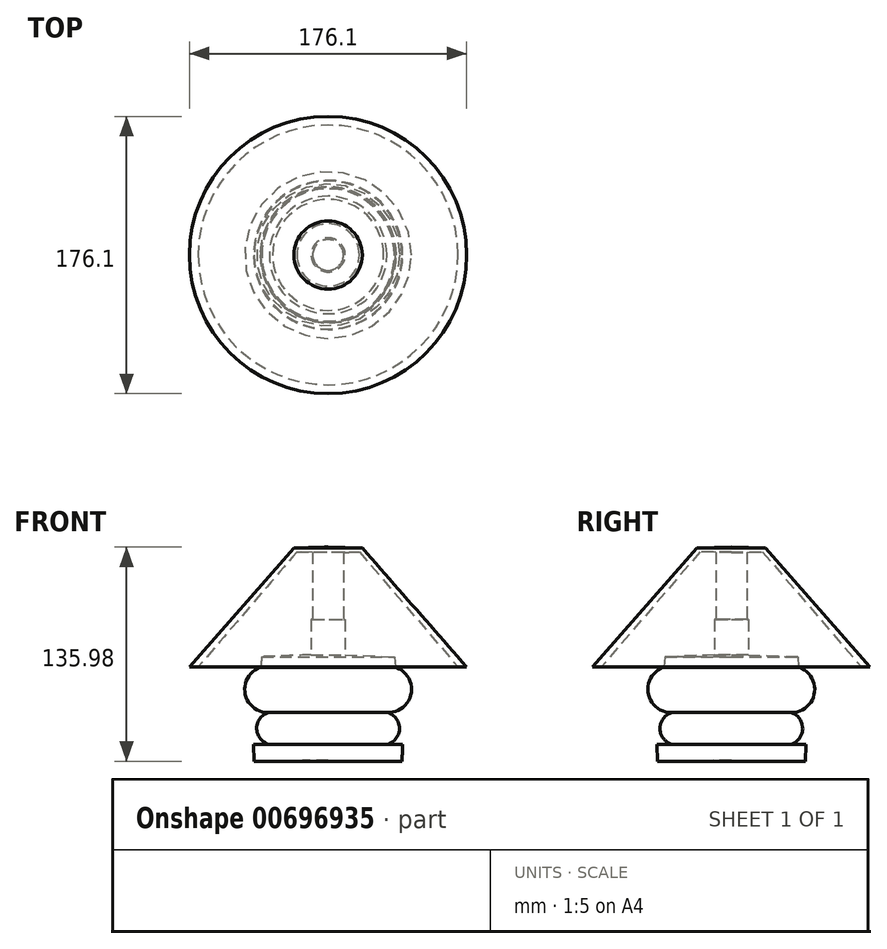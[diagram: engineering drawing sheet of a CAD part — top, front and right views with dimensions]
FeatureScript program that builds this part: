
annotation { "Feature Type Name" : "Feature", "Feature Type Description" : "" }
export const myFeature = defineFeature(function(context is Context, id is Id, definition is map)
    precondition{}
    {
        {
            var Q0;
            Q0=qCreatedBy(makeId("Front.planeOp"),FACE);
            var sketch = newSketch(context, id + "F0", { "sketchPlane" : qUnion([Q0])});
            skLineSegment(sketch, "E0", {"start": v(-88.05, 0) * mm, "end": v(-21.7, 75.44) * mm});
            skLineSegment(sketch, "E1", {"start": v(-21.7, 75.44) * mm, "end": v(0, 76.1) * mm});
            skLineSegment(sketch, "E2", {"start": v(0, 76.1) * mm, "end": v(0, 0) * mm});
            skLineSegment(sketch, "E3", {"start": v(0, 0) * mm, "end": v(0, -59.35) * mm});
            skLineSegment(sketch, "E4", {"start": v(0, -59.35) * mm, "end": v(-46.93, -59.88) * mm});
            skLineSegment(sketch, "E5", {"start": v(-46.93, -59.88) * mm, "end": v(-47.4, -49.08) * mm});
            skLineSegment(sketch, "E6", {"start": v(-47.4, -49.08) * mm, "end": v(-35.25, -49.58) * mm});
            skArc(sketch, "E7", {"start": v(-35.25, -28.54) * mm, "mid": v(-45.34, -39.06) * mm, "end": v(-35.25, -49.58) * mm});
            skArc(sketch, "E8", {"start": v(-34.81, 0) * mm, "mid": v(-53, -14) * mm, "end": v(-35.25, -28.54) * mm});
            skLineSegment(sketch, "E9", {"start": v(-33.61, -0.05) * mm, "end": v(-88.05, 0) * mm});
            skLineSegment(sketch, "E10", {"start": v(0, 110.7) * mm, "end": v(0, -82.27) * mm, "construction": true});
            skSolve(sketch);
        }
        {
            var Q0;
            Q0 = qSketchRegion(id + "F0", true);
            var Q1;
            Q1=sQuery(id+"F0.wireOp",EDGE,"E10");
            revolve(context, id + "F1", {"entities" : qUnion([Q0]), "axis" : qUnion([Q1]), "revolveType" : RevolveType.FULL});
        }
        {
            var Q0;
            Q0=qCreatedBy(makeId("Front.planeOp"),FACE);
            var sketch = newSketch(context, id + "F2", { "sketchPlane" : qUnion([Q0])});
            skLineSegment(sketch, "E11", {"start": v(-90.33, -9.16) * mm, "end": v(-19.82, 73) * mm});
            skLineSegment(sketch, "E12", {"start": v(-19.82, 73) * mm, "end": v(0, 72.54) * mm});
            skLineSegment(sketch, "E13", {"start": v(0, 72.54) * mm, "end": v(0, 30.38) * mm});
            skLineSegment(sketch, "E14", {"start": v(0, 30.38) * mm, "end": v(-10.81, 30) * mm});
            skLineSegment(sketch, "E15", {"start": v(-10.81, 30) * mm, "end": v(-10.81, 7.68) * mm});
            skLineSegment(sketch, "E16", {"start": v(-10.81, 7.68) * mm, "end": v(-42.17, 6.44) * mm});
            skLineSegment(sketch, "E17", {"start": v(-42.17, 6.44) * mm, "end": v(-42.8, -0.43) * mm});
            skLineSegment(sketch, "E18", {"start": v(-42.8, -0.43) * mm, "end": v(-49.95, -0.43) * mm});
            skLineSegment(sketch, "E19", {"start": v(-49.95, -0.43) * mm, "end": v(-60.2, -30.5) * mm});
            skLineSegment(sketch, "E20", {"start": v(-60.2, -30.5) * mm, "end": v(-90.33, -9.16) * mm});
            skSolve(sketch);
        }
        {
            var Q0;
            Q0=makeQuery(id+"F2.imprint","IMPRINT",FACE,{"disambiguationData":[TD([[makeQuery(id+"F2.imprint","IMPRINT",EDGE,{"derivedFrom":sQuery(id+"F2.wireOp",EDGE,"E11")}),-1.0]])]});
            var Q1;
            Q1=sQuery(id+"F2.wireOp",EDGE,"E13");
            revolve(context, id + "F3", {"operationType" : NewBodyOperationType.REMOVE, "entities" : qUnion([Q0]), "axis" : qUnion([Q1]), "revolveType" : RevolveType.FULL, "oppositeDirection" : true});
        }
        {
            var Q0;
            Q0=qCreatedBy(makeId("Top.planeOp"),FACE);
            var sketch = newSketch(context, id + "F4", { "sketchPlane" : qUnion([Q0])});
            skCircle(sketch, "E21", {"center": v(0, 0) * mm, "radius": 9.8 * mm});
            skSolve(sketch);
        }
        {
            var Q0;
            Q0 = qSketchRegion(id + "F4", true);
            extrude(context, id + "F5", {"entities" : qUnion([Q0]), "operationType" : NewBodyOperationType.ADD, "depth" : 75 * mm, "offsetDistance" : 25.4 * mm});
        }
    });
